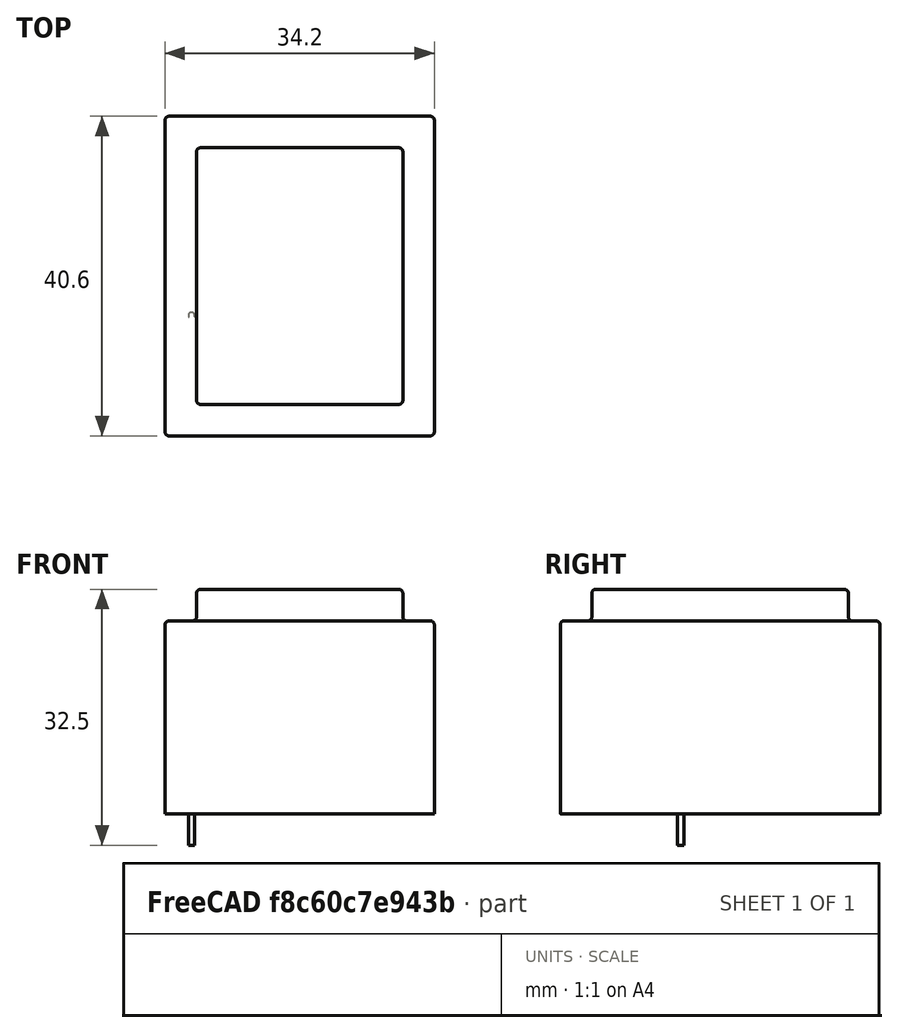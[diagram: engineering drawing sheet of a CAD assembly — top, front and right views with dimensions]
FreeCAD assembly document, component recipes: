
FREECAD ASSEMBLY — COMPONENT RECIPES ("TRANSFORMER_NF_GERTH_387.XX")

This assembly document has 4 components, labeled P0..P3 below (a component is one placed body or linked part). 4 of them carry a construction recipe — the FreeCAD feature program that regenerates the part from scratch, quoted from this document or its linked companion documents; the rest are supplied as boundary geometry only. No exploded tour is included for this assembly.
COMPONENT P0 — recipe-attached ("Gehaeuse", modeled in this document).
Construction recipe (the document's own serialized feature program — sketch geometry with constraints, then the solid features built on it; lengths are millimeters unless a unit is written):

FEATURE [Sketcher::SketchObject] Sketch
  MapMode = 5
  Support = -> [XY_Plane]
  sketch-geometry (4):
    g0: LineSegment StartX=-17.1 StartY=20.3 StartZ=0 EndX=17.1 EndY=20.3 EndZ=0
    g1: LineSegment StartX=17.1 StartY=20.3 StartZ=0 EndX=17.1 EndY=-20.3 EndZ=0
    g2: LineSegment StartX=17.1 StartY=-20.3 StartZ=0 EndX=-17.1 EndY=-20.3 EndZ=0
    g3: LineSegment StartX=-17.1 StartY=-20.3 StartZ=0 EndX=-17.1 EndY=20.3 EndZ=0
  constraints (10):
    c: Coincident(g0,g1)
    c: Coincident(g1,g2)
    c: Coincident(g2,g3)
    c: Coincident(g3,g0)
    c: Horizontal(g2)
    c: Vertical(g3)
    c: DistanceY(g1,g1) = 40.6
    c: DistanceX(g0,g0) = 34.2
    c: Symmetric(g0,g1,g-1)
    c: Symmetric(g0,g0,g-2)
FEATURE [PartDesign::Pad] Pad
  Length = 24.5
  Length2 = 100
  Profile = -> Sketch
  Type = 0
FEATURE [Sketcher::SketchObject] Sketch001
  MapMode = 5
  Placement = pos=(0,0,24.5) rot=(0,0,1;0rad)
  Support = -> [Pad]
  sketch-geometry (4):
    g0: LineSegment StartX=-13.1 StartY=16.3 StartZ=0 EndX=13.1 EndY=16.3 EndZ=0
    g1: LineSegment StartX=13.1 StartY=16.3 StartZ=0 EndX=13.1 EndY=-16.3 EndZ=0
    g2: LineSegment StartX=13.1 StartY=-16.3 StartZ=0 EndX=-13.1 EndY=-16.3 EndZ=0
    g3: LineSegment StartX=-13.1 StartY=-16.3 StartZ=0 EndX=-13.1 EndY=16.3 EndZ=0
  constraints (10):
    c: Coincident(g0,g1)
    c: Coincident(g1,g2)
    c: Coincident(g2,g3)
    c: Coincident(g3,g0)
    c: Horizontal(g0)
    c: Vertical(g1)
    c: DistanceY(g1,g1) = 32.6
    c: DistanceX(g0,g0) = 26.2
    c: Symmetric(g0,g2,g-1)
    c: Symmetric(g2,g1,g-2)
FEATURE [PartDesign::Pad] Pad001
  BaseFeature = -> Pad
  Length = 4
  Length2 = 100
  Profile = -> Sketch001
  Type = 0
FEATURE [PartDesign::Fillet] Fillet
  Base = -> Pad001 [Edge23,Edge24,Edge21,Edge19,Edge4,Edge10,Edge12,Edge7,Edge22,Edge15,Edge20,Edge14,Edge18,Edge13,Edge17,Edge16,Edge1,Edge8,Edge2,Edge5]
  BaseFeature = -> Pad001
  Radius = 0.5
  SupportTransform = true
FEATURE [PartDesign::Body] Body  label="Gehaeuse"
  Group = -> [Sketch,Pad,Sketch001,Pad001,Fillet]
  Origin = -> Origin
  Tip = -> Fillet
COMPONENT P1 — recipe-attached ("Pin 7", modeled in this document).
Construction recipe (the document's own serialized feature program — sketch geometry with constraints, then the solid features built on it; lengths are millimeters unless a unit is written):

FEATURE [PartDesign::ShapeBinder] CopyFillet
  TraceSupport = false
FEATURE [Sketcher::SketchObject] Sketch002
  MapMode = 5
  Placement = pos=(0,0,0) rot=(1,0,0;3.14159rad)
  Support = -> [CopyFillet]
  sketch-geometry (1):
    g0: Circle CenterX=0 CenterY=0 CenterZ=0 NormalX=0 NormalY=0 NormalZ=1 AngleXU=0 Radius=0.4
  constraints (2):
    c: Diameter(g0) = 0.8
    c: Coincident(g-1,g0)
FEATURE [PartDesign::Pad] Pad002
  Length = 4
  Length2 = 100
  Profile = -> Sketch002
  Type = 0
FEATURE [PartDesign::Body] Body001  label="Pin 9"
  Group = -> [CopyFillet,Sketch002,Pad002]
  Origin = -> Origin001
  Placement = pos=(-13.75,-5,0) rot=(0,0,1;0rad)
  Tip = -> Pad002
COMPONENT P2 — same part as P1; its construction recipe is shown at P1.
COMPONENT P3 — same part as P1; its construction recipe is shown at P1.
PROVENANCE & LICENSES
A FreeCAD (.FCStd) document from a public repository crawl; recipes are the document's own serialized feature recipes (and, for linked parts, companion documents' recipes).
License: as declared in the source repository (recorded in the dataset sidecar).
